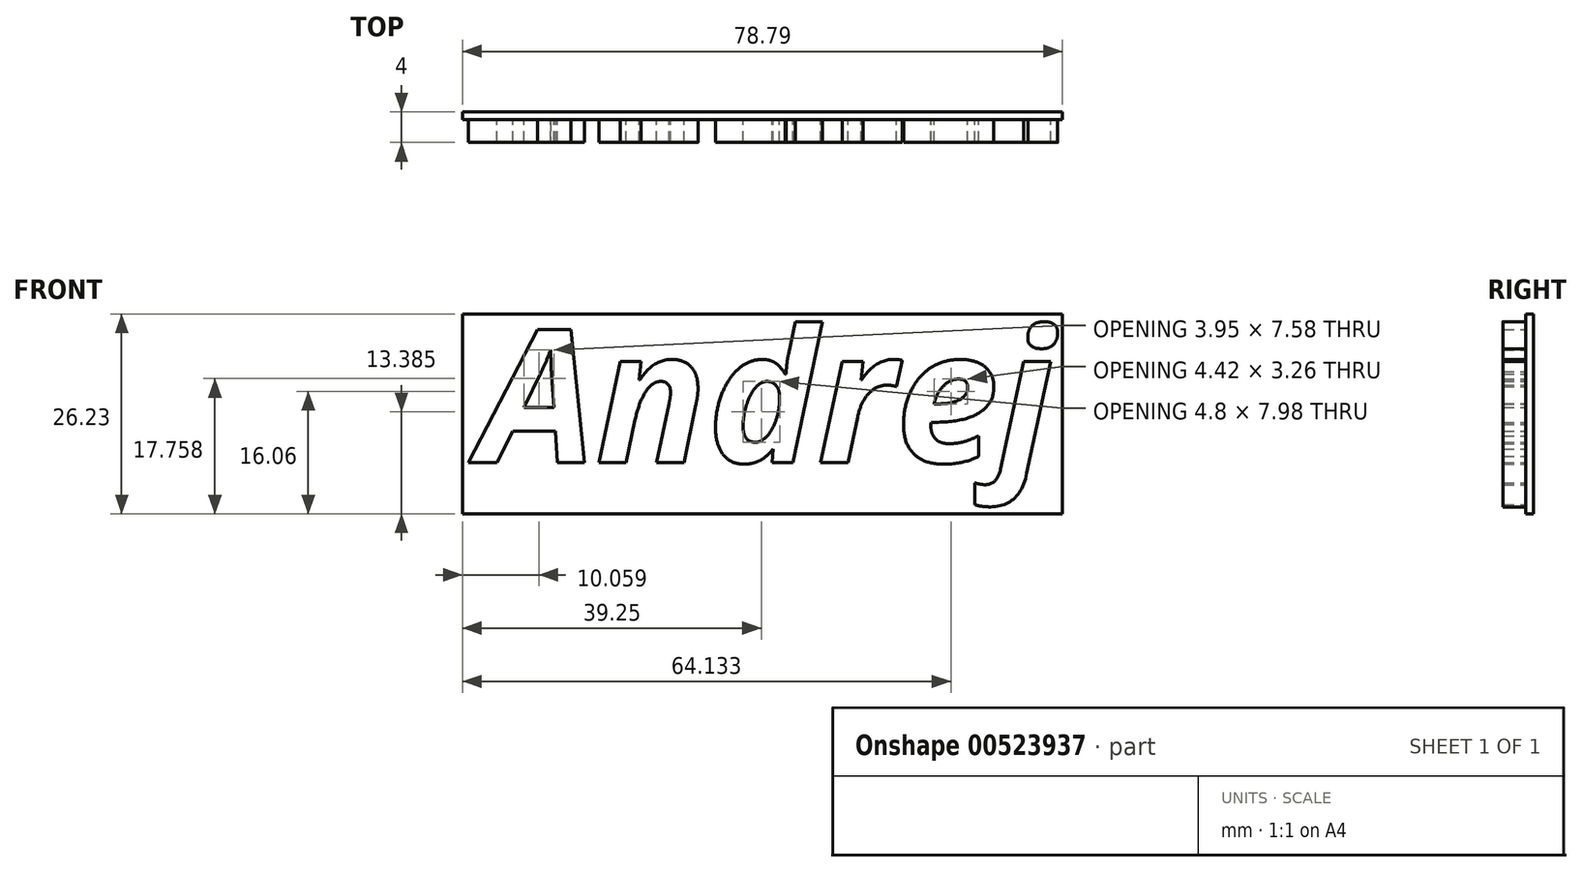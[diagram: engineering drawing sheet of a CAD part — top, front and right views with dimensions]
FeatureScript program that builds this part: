
annotation { "Feature Type Name" : "Feature", "Feature Type Description" : "" }
export const myFeature = defineFeature(function(context is Context, id is Id, definition is map)
    precondition{}
    {
        {
            var Q0;
            Q0=qCreatedBy(makeId("Front.planeOp"),FACE);
            var sketch = newSketch(context, id + "F0", { "sketchPlane" : qUnion([Q0])});
            skText(sketch, "E0", { "text": "Andrej", "fontName": "OpenSans-BoldItalic.ttf"});
            const initialGuessF0  = {"E0": [-0.04475, -0.00012, 1, 0, 0.0175]};
            skSetInitialGuess(sketch, initialGuessF0);
            skSolve(sketch);
        }
        {
            var Q0;
            Q0=qSketchRegion(id+"F0",true);
            extrude(context, id + "F1", {"entities" : qUnion([Q0]), "depth" : 3 * mm});
        }
        {
            var Q0;
            Q0=makeQuery(id+"F0.imprint","IMPRINT",FACE,{"disambiguationData":[TD([[makeQuery(id+"F0.imprint","IMPRINT",EDGE,{"derivedFrom":sQuery(id+"F0.wireOp",EDGE,"E0.sketch_text.stroke-36")}),-1.0]])]});
            var sketch = newSketch(context, id + "F2", { "sketchPlane" : qUnion([Q0])});
            skLineSegment(sketch, "E1.bottom", {"start": v(-46.97, 19.36) * mm, "end": v(31.82, 19.36) * mm});
            skLineSegment(sketch, "E1.top", {"start": v(-46.97, -6.87) * mm, "end": v(31.82, -6.87) * mm});
            skLineSegment(sketch, "E1.left", {"start": v(-46.97, 19.36) * mm, "end": v(-46.97, -6.87) * mm});
            skLineSegment(sketch, "E1.right", {"start": v(31.82, 19.36) * mm, "end": v(31.82, -6.87) * mm});
            skSolve(sketch);
        }
        {
            var Q0;
            Q0=qSketchRegion(id+"F2",true);
            extrude(context, id + "F3", {"entities" : qUnion([Q0]), "oppositeDirection" : true, "depth" : 1 * mm, "offsetDistance" : 25 * mm});
        }
    });
